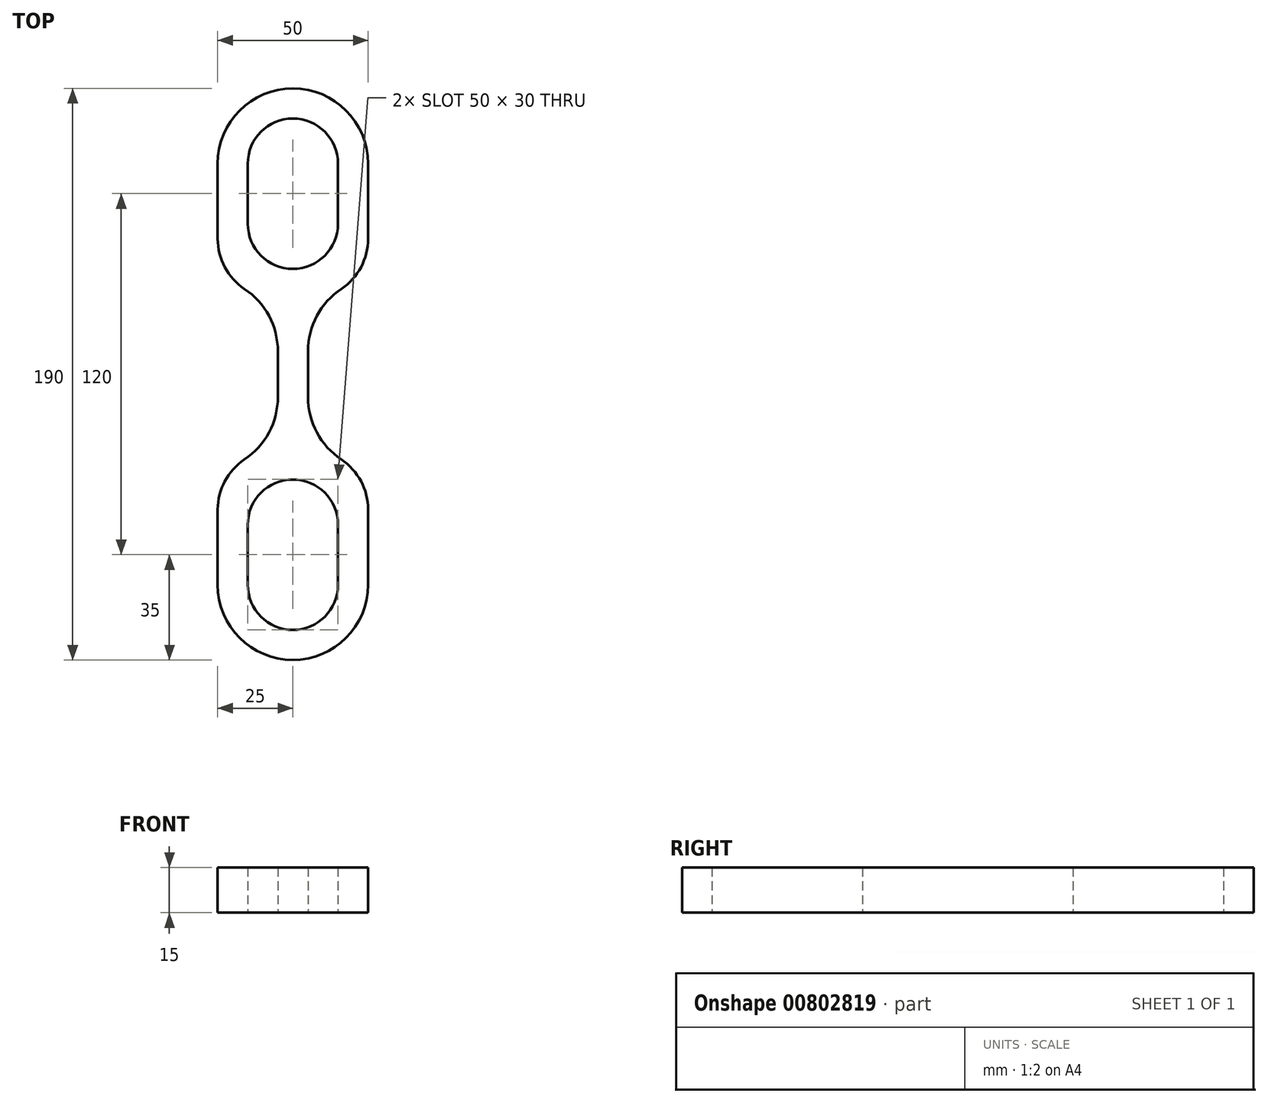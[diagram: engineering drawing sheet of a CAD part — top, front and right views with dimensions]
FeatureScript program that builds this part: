
annotation { "Feature Type Name" : "Feature", "Feature Type Description" : "" }
export const myFeature = defineFeature(function(context is Context, id is Id, definition is map)
    precondition{}
    {
        {
            var Q0;
            Q0=qCreatedBy(makeId("Top.planeOp"),FACE);
            var sketch = newSketch(context, id + "F0", { "sketchPlane" : qUnion([Q0])});
            skLineSegment(sketch, "E0.left", {"start": v(25, 70) * mm, "end": v(25, 45) * mm});
            skLineSegment(sketch, "E0.right", {"start": v(-25, 70) * mm, "end": v(-25, 45) * mm});
            skPoint(sketch, "E0.middle", {"position": v(0, 0) * mm});
            skArc(sketch, "E1", {"start": v(-25, -70) * mm, "mid": v(0, -95) * mm, "end": v(25, -70) * mm});
            skPoint(sketch, "E2.orphan", {"position": v(25, -75) * mm});
            skPoint(sketch, "E3.orphan", {"position": v(-25, -75) * mm});
            skArc(sketch, "E4.MirrorCS", {"start": v(-25, 70) * mm, "mid": v(0, 95) * mm, "end": v(25, 70) * mm});
            skPoint(sketch, "E5.orphan", {"position": v(-25, 75) * mm});
            skPoint(sketch, "E6.orphan", {"position": v(25, 75) * mm});
            skArc(sketch, "E7.0", {"start": v(-15, -70) * mm, "mid": v(0, -85) * mm, "end": v(15, -70) * mm});
            skLineSegment(sketch, "E8.0", {"start": v(-15, -50) * mm, "end": v(-15, -70) * mm});
            skLineSegment(sketch, "E9.0", {"start": v(15, -50) * mm, "end": v(15, -70) * mm});
            skLineSegment(sketch, "E10", {"start": v(-15, -60) * mm, "end": v(15, -60) * mm, "construction": true});
            skArc(sketch, "E11.MirrorCS", {"start": v(-15, -50) * mm, "mid": v(0, -35) * mm, "end": v(15, -50) * mm});
            skArc(sketch, "E12.MirrorCS", {"start": v(-15, 50) * mm, "mid": v(0, 35) * mm, "end": v(15, 50) * mm});
            skLineSegment(sketch, "E13.MirrorCS", {"start": v(-15, 50) * mm, "end": v(-15, 70) * mm});
            skLineSegment(sketch, "E14.MirrorCS", {"start": v(15, 50) * mm, "end": v(15, 70) * mm});
            skArc(sketch, "E15.MirrorCS", {"start": v(-15, 70) * mm, "mid": v(0, 85) * mm, "end": v(15, 70) * mm});
            skLineSegment(sketch, "E16.bottom", {"start": v(10, -25) * mm, "end": v(5, -25) * mm, "construction": true});
            skLineSegment(sketch, "E16.right", {"start": v(5, -7.58) * mm, "end": v(5, 0) * mm});
            skPoint(sketch, "E16.middle", {"position": v(15, -12.5) * mm});
            skLineSegment(sketch, "E17.MirrorCS", {"start": v(-5, -35) * mm, "end": v(-5, -25) * mm, "construction": true});
            skLineSegment(sketch, "E18.trimOffspring", {"start": v(25, -45) * mm, "end": v(25, -70) * mm});
            skLineSegment(sketch, "E19.trimOffspring", {"start": v(-25, -45) * mm, "end": v(-25, -70) * mm});
            skPoint(sketch, "E20.visualSharp", {"position": v(25, -25) * mm});
            skArc(sketch, "E20.filletArc", {"start": v(25, -45) * mm, "mid": v(22.64, -35.57) * mm, "end": v(16.11, -28.37) * mm});
            skArc(sketch, "E21.filletArc", {"start": v(5, -7.58) * mm, "mid": v(7.95, -19.37) * mm, "end": v(16.11, -28.37) * mm});
            skArc(sketch, "E22.MirrorCS", {"start": v(-5, -7.58) * mm, "mid": v(-7.95, -19.37) * mm, "end": v(-16.11, -28.37) * mm});
            skArc(sketch, "E23.MirrorCS", {"start": v(-25, -45) * mm, "mid": v(-22.64, -35.57) * mm, "end": v(-16.11, -28.37) * mm});
            skLineSegment(sketch, "E24.trimOffspring", {"start": v(-5, -7.58) * mm, "end": v(-5, 0) * mm});
            skPoint(sketch, "E25.orphan", {"position": v(-25, -25) * mm});
            skArc(sketch, "E26.MirrorCS", {"start": v(25, 45) * mm, "mid": v(22.64, 35.57) * mm, "end": v(16.11, 28.37) * mm});
            skArc(sketch, "E27.MirrorCS", {"start": v(5, 7.58) * mm, "mid": v(7.95, 19.37) * mm, "end": v(16.11, 28.37) * mm});
            skArc(sketch, "E28.MirrorCS", {"start": v(-5, 7.58) * mm, "mid": v(-7.95, 19.37) * mm, "end": v(-16.11, 28.37) * mm});
            skArc(sketch, "E29.MirrorCS", {"start": v(-25, 45) * mm, "mid": v(-22.64, 35.57) * mm, "end": v(-16.11, 28.37) * mm});
            skLineSegment(sketch, "E30.trimOffspring", {"start": v(5, 7.58) * mm, "end": v(5, 0) * mm});
            skPoint(sketch, "E31.MirrorCS.end.orphan", {"position": v(5, 25) * mm});
            skPoint(sketch, "E32.orphan", {"position": v(25, 25) * mm});
            skLineSegment(sketch, "E33.trimOffspring", {"start": v(-5, 7.58) * mm, "end": v(-5, 0) * mm});
            skPoint(sketch, "E34.MirrorCS.start.orphan", {"position": v(-5, 35) * mm});
            skPoint(sketch, "E35.orphan", {"position": v(-5, 25) * mm});
            skPoint(sketch, "E36.orphan", {"position": v(-25, 25) * mm});
            skSolve(sketch);
        }
        {
            var Q0;
            Q0=makeQuery(id+"F0.imprint","IMPRINT",FACE,{"disambiguationData":[TD([[makeQuery(id+"F0.imprint","IMPRINT",EDGE,{"derivedFrom":sQuery(id+"F0.wireOp",EDGE,"E0.left")}),-1.0]])]});
            extrude(context, id + "F1", {"entities" : qUnion([Q0]), "depth" : 15 * mm, "offsetDistance" : 25 * mm});
        }
    });
